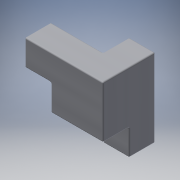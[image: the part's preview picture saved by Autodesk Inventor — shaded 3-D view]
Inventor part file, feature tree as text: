
AUTODESK INVENTOR PART (.ipt)
format: ipt  version: 2016 (Build 200138000, 138)  size: 179,200 bytes
history: native  units: in
note: dims shown in document units (in); Inventor stores cm internally (conversion verified against a paired STEP export)
features: plane x8, extrude x2, other x1, fillet x1, sketch x1
ambient origin geometry x8: Origin, YZ Plane, XZ Plane, XY Plane, X Axis, Y Axis, Z Axis, Center Point
bodies: Solid1 (feature_tree)
feature tree (13):
  other  "Cube Master.ipt"
  extrude  "Extrusion1"  Depth=0.3937in
  extrude  "Extrusion2"  Depth=0.0193in TaperAngle=0.0deg
  fillet  "Fillet1"  Radius=1.0in
  sketch  "Sketch1"  dims[d0=0.3937in d1=0.3937in d2=1.0in d3=0.0in d4=1.0in d5=0.0in d7=0.0193in d8=0.0193in]
  plane  "Work Plane1"
  plane  "Work Plane2"
  plane  "Work Plane3"
  plane  "Work Plane4"
  plane  "Work Plane5"
  plane  "Work Plane6"
  plane  "Work Plane7"
  plane  "Work Plane8"
